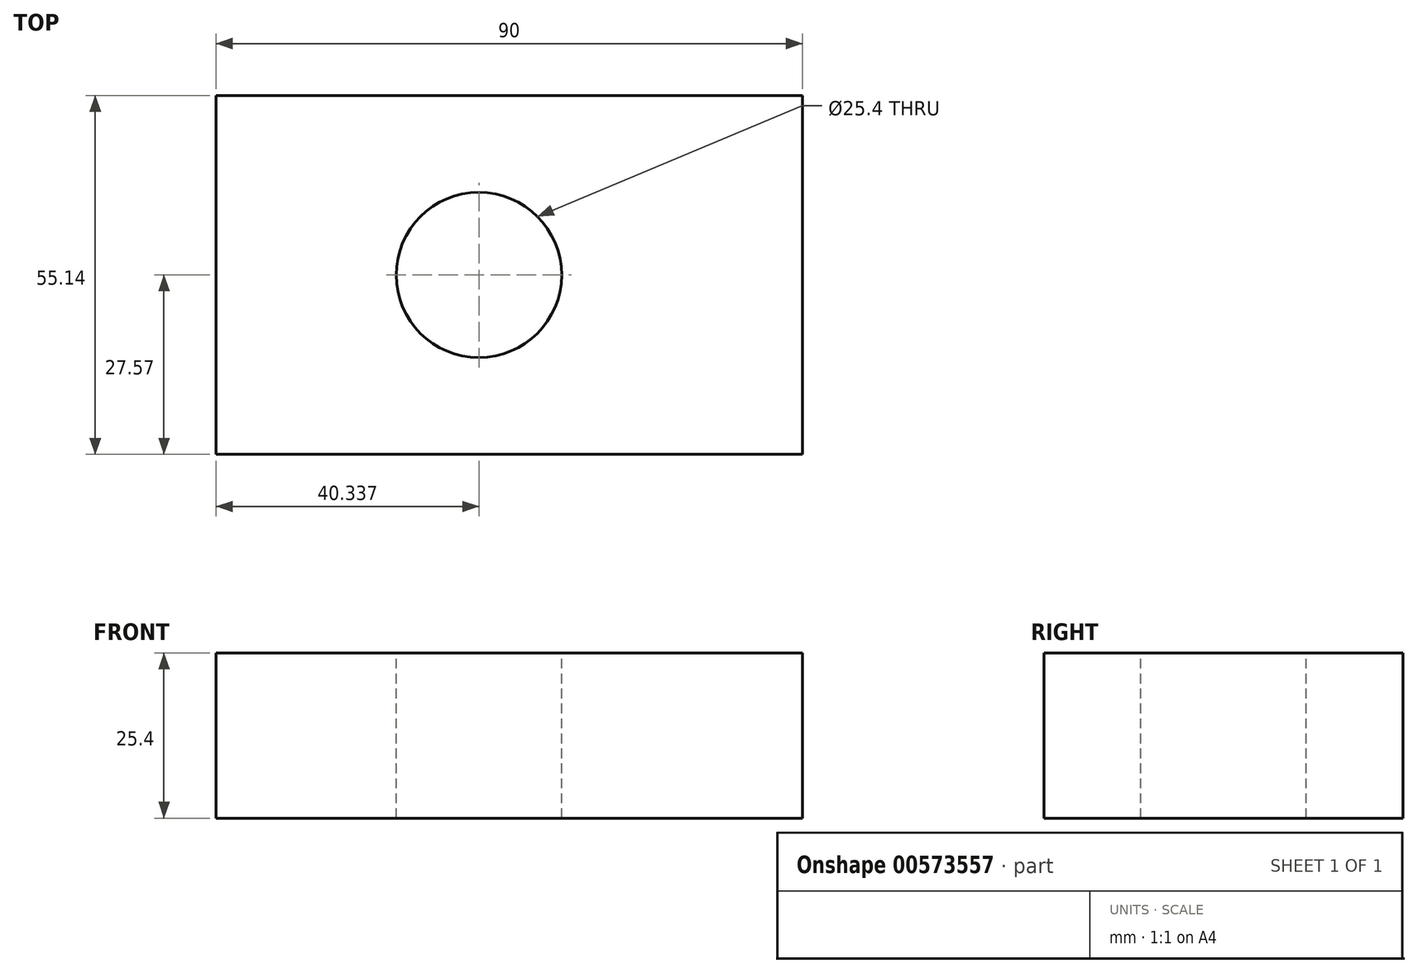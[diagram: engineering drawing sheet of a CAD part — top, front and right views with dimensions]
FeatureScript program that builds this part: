
annotation { "Feature Type Name" : "Feature", "Feature Type Description" : "" }
export const myFeature = defineFeature(function(context is Context, id is Id, definition is map)
    precondition{}
    {
        {
            var Q0;
            Q0=qCreatedBy(makeId("Top.planeOp"),FACE);
            var sketch = newSketch(context, id + "F0", { "sketchPlane" : qUnion([Q0])});
            skLineSegment(sketch, "E0.bottom", {"start": v(0, 0) * mm, "end": v(90, 0) * mm});
            skLineSegment(sketch, "E0.top", {"start": v(0, -55.14) * mm, "end": v(90, -55.14) * mm});
            skLineSegment(sketch, "E0.left", {"start": v(0, 0) * mm, "end": v(0, -55.14) * mm});
            skLineSegment(sketch, "E0.right", {"start": v(90, 0) * mm, "end": v(90, -55.14) * mm});
            skSolve(sketch);
        }
        {
            var Q0;
            Q0 = qSketchRegion(id + "F0", true);
            extrude(context, id + "F1", {"entities" : qUnion([Q0]), "depth" : 25.4 * mm, "offsetDistance" : 25.4 * mm});
        }
        {
            var Q0;
            Q0=makeQuery(id+"F1.opExtrude","CAP_FACE",FACE,{"disambiguationData":[OSD([sQuery(id+"F0.wireOp",EDGE,"E0.bottom"),sQuery(id+"F0.wireOp",EDGE,"E0.top"),sQuery(id+"F0.wireOp",EDGE,"E0.left"),sQuery(id+"F0.wireOp",EDGE,"E0.right")])],"isStart":false});
            var sketch = newSketch(context, id + "F2", { "sketchPlane" : qUnion([Q0])});
            skCircle(sketch, "E1", {"center": v(40.34, -27.57) * mm, "radius": 12.7 * mm});
            skPoint(sketch, "E1.centerSnap0", {"position": v(0, -27.57) * mm});
            skSolve(sketch);
        }
        {
            var Q0;
            Q0=makeQuery(id+"F2.imprint","IMPRINT",FACE,{"disambiguationData":[TD([[makeQuery(id+"F2.imprint","IMPRINT",EDGE,{"derivedFrom":sQuery(id+"F2.wireOp",EDGE,"E1")}),1.0]])]});
            extrude(context, id + "F3", {"entities" : qUnion([Q0]), "operationType" : NewBodyOperationType.REMOVE, "endBound" : BoundingType.UP_TO_NEXT, "oppositeDirection" : true, "depth" : 25.4 * mm, "offsetDistance" : 25.4 * mm});
        }
    });
